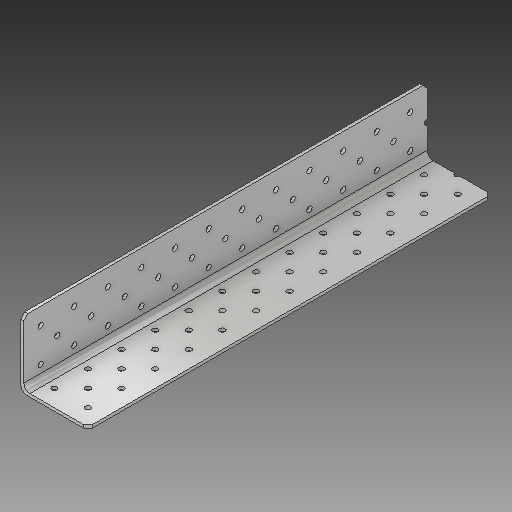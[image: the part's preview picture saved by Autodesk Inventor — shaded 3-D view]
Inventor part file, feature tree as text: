
AUTODESK INVENTOR PART (.ipt)
format: ipt  version: 2017 (Build 210142000, 142)  size: 252,928 bytes
history: native  units: in
note: dims shown in document units (in); Inventor stores cm internally (conversion verified against a paired STEP export)
features: sketch x5, hole x4, projected_geometry x4, other x3, pattern_linear x2, extrude x1, chamfer x1, fillet x1
ambient origin geometry x8: Origin, YZ Plane, XZ Plane, XY Plane, X Axis, Y Axis, Z Axis, Center Point
bodies: Solid1 (feature_tree)
feature tree (21):
  other  "Table"
  other  "versaframe_angle-1x1"
  other  "versaframe_angle-2x2"
  extrude  "Extrusion1"  TaperAngle=0.0deg  [1 undecoded]
  hole  "Hole1"  [1 undecoded]
  hole  "Hole2"  [1 undecoded]
  hole  "Hole3"  [1 undecoded]
  hole  "Hole4"  [1 undecoded]
  chamfer  "Chamfer1"  Distance=0.5in
  fillet  "Fillet1"  Radius=0.5in
  pattern_linear  "Rectangular Pattern1"  Spacing1=0.5in  [1 undecoded]
  pattern_linear  "Rectangular Pattern2"  Spacing1=0.5in  [1 undecoded]
  sketch  "Sketch1"  dims[d1=0.09in d3=0.0in]
  sketch  "Sketch2"  dims[d4=2.0in d5=1.0in]
  projected_geometry  "Projected Loop1"
  sketch  "Sketch3"  dims[d7=0.161in d8=0.75in d9=0.375in d10=0.25in d11=0.5635in d12=1.0in d13=0.8108in d14=2.0in]
  projected_geometry  "Projected Loop2"
  sketch  "Sketch4"  dims[d15=1.0in d16=1.0in]
  projected_geometry  "Projected Loop3"
  sketch  "Sketch5"  dims[d17=0.161in d18=0.75in d19=0.375in d20=0.25in d21=0.5635in d22=1.0in d23=0.8108in d24=0.5in d25=0.5in d26=0.5in d27=0.161in d28=0.75in d29=0.375in d30=0.25in d31=0.5635in d32=1.0in d33=0.8108in d34=0.5in d35=0.5in d36=0.5in d37=0.161in d38=0.75in d39=0.375in d40=0.25in d41=0.5635in d42=1.0in d43=0.8108in d44=0.125in d45=0.125in d46=45.0deg d47=0.18in d48=5.1181in d50=1.0in d51=5.1181in d53=1.0in]
  projected_geometry  "Projected Loop4"
note: 7 required parameter values undecoded (feature->parameter linkage not recoverable at this tier; creation-order binding heuristic only, values carry confidence <= 0.55)
